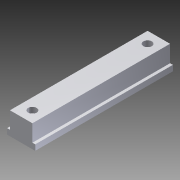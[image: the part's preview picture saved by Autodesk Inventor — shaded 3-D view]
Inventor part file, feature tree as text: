
AUTODESK INVENTOR PART (.ipt)
format: ipt  version: 2012 (Build 160160000, 160)  size: 96,256 bytes
history: native  units: in
note: dims shown in document units (in); Inventor stores cm internally (conversion verified against a paired STEP export)
features: sketch x2, extrude x1, hole x1
ambient origin geometry x8: Origin, YZ Plane, XZ Plane, XY Plane, X Axis, Y Axis, Z Axis, Center Point
bodies: Solid1 (feature_tree)
feature tree (4):
  extrude  "Extrusion1"  Depth=1.0in
  hole  "Hole1"  [1 undecoded]
  sketch  "Sketch1"  dims[d0=1.25in d1=1.0in]
  sketch  "Sketch2"  dims[d2=0.25in d3=0.125in d4=6.125in d5=0.0in d6=0.5in d7=0.5in d8=0.5in d9=0.5in d10=0.25in d11=0.75in d12=0.375in d13=0.25in d14=0.5635in d15=1.0in d16=0.8108in]
note: 1 required parameter value undecoded (feature->parameter linkage not recoverable at this tier; creation-order binding heuristic only, values carry confidence <= 0.55)
